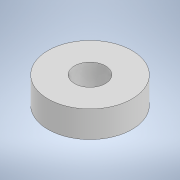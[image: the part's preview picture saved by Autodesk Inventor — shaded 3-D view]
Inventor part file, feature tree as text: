
AUTODESK INVENTOR PART (.ipt)
format: ipt  version: 2020 (Build 240168000, 168)  size: 212,992 bytes
history: native  units: mm
features: other x1, extrude x1, sketch x1
ambient origin geometry x8: Origin, YZ Plane, XZ Plane, XY Plane, X Axis, Y Axis, Z Axis, Center Point
bodies: Body1 (feature_tree)
feature tree (3):
  other  "Твердое тело1"
  extrude  "Выдавливание1"  Depth=3.5mm
  sketch  "Эскиз1"
